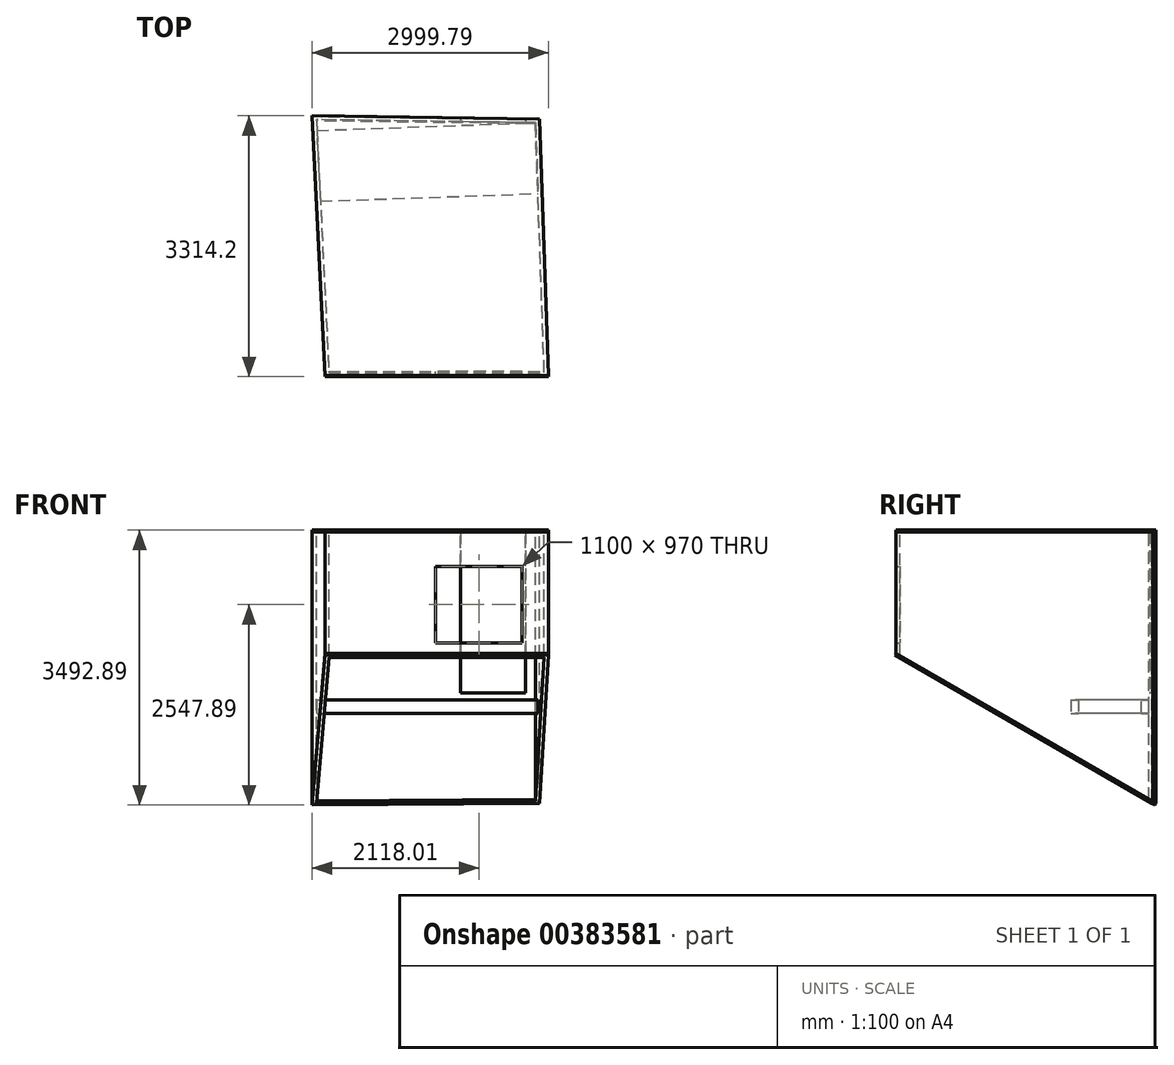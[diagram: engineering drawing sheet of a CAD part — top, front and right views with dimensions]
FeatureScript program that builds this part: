
annotation { "Feature Type Name" : "Feature", "Feature Type Description" : "" }
export const myFeature = defineFeature(function(context is Context, id is Id, definition is map)
    precondition{}
    {
        {
            var Q0;
            Q0=qCreatedBy(makeId("Top.planeOp"),FACE);
            var sketch = newSketch(context, id + "F0", { "sketchPlane" : qUnion([Q0])});
            skLineSegment(sketch, "E0", {"start": v(0, 0) * mm, "end": v(2735, 0) * mm});
            skLineSegment(sketch, "E1", {"start": v(2735, 0) * mm, "end": v(2624.33, 3163.06) * mm});
            skLineSegment(sketch, "E2", {"start": v(2624.33, 3163.06) * mm, "end": v(-160.4, 3200.98) * mm});
            skLineSegment(sketch, "E3", {"start": v(-160.4, 3200.98) * mm, "end": v(0, 0) * mm});
            skLineSegment(sketch, "E4", {"start": v(2624.33, 3163.06) * mm, "end": v(0, 0) * mm, "construction": true});
            skLineSegment(sketch, "E5.0", {"start": v(-47.56, -50) * mm, "end": v(2786.78, -50) * mm});
            skLineSegment(sketch, "E5.1", {"start": v(-213.01, 3251.7) * mm, "end": v(-47.56, -50) * mm});
            skLineSegment(sketch, "E5.2", {"start": v(2672.64, 3212.41) * mm, "end": v(-213.01, 3251.7) * mm});
            skLineSegment(sketch, "E5.3", {"start": v(2786.78, -50) * mm, "end": v(2672.64, 3212.41) * mm});
            skSolve(sketch);
        }
        {
            var Q0;
            Q0=makeQuery(id+"F0.imprint","IMPRINT",FACE,{"disambiguationData":[TD([[makeQuery(id+"F0.imprint","IMPRINT",EDGE,{"derivedFrom":sQuery(id+"F0.wireOp",EDGE,"E0")}),-1.0]])]});
            extrude(context, id + "F1", {"entities" : qUnion([Q0]), "oppositeDirection" : true, "depth" : 4110 * mm});
        }
        {
            var Q0;
            Q0=makeQuery(id+"F1.opExtrude","SWEPT_FACE",FACE,{"disambiguationData":[OSD([sQuery(id+"F0.wireOp",EDGE,"E5.0")])]});
            var sketch = newSketch(context, id + "F2", { "sketchPlane" : qUnion([Q0])});
            skLineSegment(sketch, "E6", {"start": v(-47.56, -1540) * mm, "end": v(2786.78, -1540) * mm});
            skSolve(sketch);
        }
        {
            var Q0;
            Q0=sQuery(id+"F2.wireOp",EDGE,"E6");
            cPlane(context, id + "F3", {"entities" : qUnion([Q0]), "cplaneType" : CPlaneType.LINE_ANGLE, "offset" : 25 * mm, "angle" : 30 * degree, "oppositeDirection" : true, "width" : 150 * mm, "height" : 150 * mm});
        }
        {
            var Q0;
            Q0=qCreatedBy(id+"F3.planeOp",FACE);
            var sketch = newSketch(context, id + "F4", { "sketchPlane" : qUnion([Q0])});
            skLineSegment(sketch, "E7.0", {"start": v(47.56, -1358.68) * mm, "end": v(-2786.78, -1358.68) * mm});
            skLineSegment(sketch, "E8.bottom", {"start": v(-2786.78, -1358.68) * mm, "end": v(1857.9, -1358.68) * mm});
            skLineSegment(sketch, "E8.top", {"start": v(-2786.78, -4651.7) * mm, "end": v(1857.9, -4651.7) * mm});
            skLineSegment(sketch, "E8.left", {"start": v(-2786.78, -1358.68) * mm, "end": v(-2786.78, -4651.7) * mm});
            skLineSegment(sketch, "E8.right", {"start": v(1857.9, -1358.68) * mm, "end": v(1857.9, -4651.7) * mm});
            skSolve(sketch);
        }
        {
            var Q0;
            Q0=makeQuery(id+"F4.imprint","IMPRINT",FACE,{"disambiguationData":[TD([[makeQuery(id+"F4.imprint","IMPRINT",EDGE,{"derivedFrom":sQuery(id+"F4.wireOp",EDGE,"E8.top")}),1.0]])]});
            extrude(context, id + "F5", {"entities" : qUnion([Q0]), "operationType" : NewBodyOperationType.REMOVE, "endBound" : BoundingType.THROUGH_ALL, "depth" : 25 * mm});
        }
        {
            var Q0;
            Q0=makeQuery(id+"F0.imprint","IMPRINT",FACE,{"disambiguationData":[TD([[makeQuery(id+"F0.imprint","IMPRINT",EDGE,{"derivedFrom":sQuery(id+"F0.wireOp",EDGE,"E0")}),1.0]])]});
            var Q1;
            Q1=makeQuery(id+"F0.imprint","IMPRINT",FACE,{"disambiguationData":[TD([[makeQuery(id+"F0.imprint","IMPRINT",EDGE,{"derivedFrom":sQuery(id+"F0.wireOp",EDGE,"E0")}),-1.0]])]});
            extrude(context, id + "F6", {"entities" : qUnion([Q0, Q1]), "depth" : 25 * mm});
        }
        {
            var Q0;
            Q0=makeQuery(id+"F5.boolean.opBoolean","COPY",FACE,{"derivedFrom":makeQuery(id+"F5.opExtrude","SWEPT_FACE",FACE,{"disambiguationData":[OSD([sQuery(id+"F4.wireOp",EDGE,"E8.bottom")])]})});
            var sketch = newSketch(context, id + "F7", { "sketchPlane" : qUnion([Q0])});
            skLineSegment(sketch, "E9", {"start": v(2672.64, -4493.8) * mm, "end": v(-213.01, -4539.18) * mm});
            skLineSegment(sketch, "E10", {"start": v(-213.01, -4539.18) * mm, "end": v(-47.56, -726.7) * mm});
            skLineSegment(sketch, "E11", {"start": v(-47.56, -726.7) * mm, "end": v(2786.78, -726.7) * mm});
            skLineSegment(sketch, "E12", {"start": v(2786.78, -726.7) * mm, "end": v(2672.64, -4493.8) * mm});
            skLineSegment(sketch, "E13.0", {"start": v(2624.33, -4436.83) * mm, "end": v(2735, -784.43) * mm});
            skLineSegment(sketch, "E14.0", {"start": v(-160.4, -4480.61) * mm, "end": v(2624.33, -4436.83) * mm});
            skLineSegment(sketch, "E15.0", {"start": v(0, -784.43) * mm, "end": v(-160.4, -4480.61) * mm});
            skLineSegment(sketch, "E16.0", {"start": v(2735, -784.43) * mm, "end": v(0, -784.43) * mm});
            skSolve(sketch);
        }
        {
            var Q0;
            Q0=makeQuery(id+"F7.imprint","IMPRINT",FACE,{"disambiguationData":[TD([[makeQuery(id+"F7.imprint","IMPRINT",EDGE,{"derivedFrom":sQuery(id+"F7.wireOp",EDGE,"E13.0")}),1.0]])]});
            var Q1;
            Q1=makeQuery(id+"F7.imprint","IMPRINT",FACE,{"disambiguationData":[TD([[makeQuery(id+"F7.imprint","IMPRINT",EDGE,{"derivedFrom":sQuery(id+"F7.wireOp",EDGE,"E9")}),1.0]])]});
            extrude(context, id + "F8", {"entities" : qUnion([Q0, Q1]), "depth" : 25 * mm});
        }
        {
            var Q0;
            Q0=makeQuery(id+"F1.opExtrude","SWEPT_FACE",FACE,{"disambiguationData":[OSD([sQuery(id+"F0.wireOp",EDGE,"E2")])]});
            var sketch = newSketch(context, id + "F9", { "sketchPlane" : qUnion([Q0])});
            skLineSegment(sketch, "E17.bottom", {"start": v(2456.02, 0) * mm, "end": v(1626.02, 0) * mm});
            skLineSegment(sketch, "E17.top", {"start": v(2456.02, -2040) * mm, "end": v(1626.02, -2040) * mm});
            skLineSegment(sketch, "E17.left", {"start": v(2456.02, 0) * mm, "end": v(2456.02, -2040) * mm});
            skLineSegment(sketch, "E17.right", {"start": v(1626.02, 0) * mm, "end": v(1626.02, -2040) * mm});
            skSolve(sketch);
        }
        {
            var Q0;
            Q0=makeQuery(id+"F9.imprint","IMPRINT",FACE,{"disambiguationData":[TD([[makeQuery(id+"F9.imprint","IMPRINT",EDGE,{"derivedFrom":sQuery(id+"F9.wireOp",EDGE,"E17.bottom")}),1.0]])]});
            extrude(context, id + "F10", {"entities" : qUnion([Q0]), "operationType" : NewBodyOperationType.REMOVE, "endBound" : BoundingType.THROUGH_ALL, "oppositeDirection" : true, "depth" : 25 * mm});
        }
        {
            var Q0;
            Q0=makeQuery(id+"F9.imprint","IMPRINT",FACE,{"disambiguationData":[TD([[makeQuery(id+"F9.imprint","IMPRINT",EDGE,{"derivedFrom":sQuery(id+"F9.wireOp",EDGE,"E17.bottom")}),1.0]])]});
            var Q1;
            {var subQ0=sQuery(id+"F0.wireOp",EDGE,"E5.2");Q1=makeQuery(id+"F6.boolean.opBoolean","MERGE",FACE,{"derivedFrom":[makeQuery(id+"F1.opExtrude","SWEPT_FACE",FACE,{"disambiguationData":[OSD([subQ0])]}),makeQuery(id+"F6.opExtrude","SWEPT_FACE",FACE,{"disambiguationData":[OSD([subQ0])]})]});}
            extrude(context, id + "F11", {"entities" : qUnion([Q0]), "endBound" : BoundingType.UP_TO_SURFACE, "oppositeDirection" : true, "endBoundEntityFace" : qUnion([Q1]), "depth" : 25 * mm});
        }
        {
            var Q0;
            Q0=makeQuery(id+"F1.opExtrude","SWEPT_FACE",FACE,{"disambiguationData":[OSD([sQuery(id+"F0.wireOp",EDGE,"E1")])]});
            var sketch = newSketch(context, id + "F12", { "sketchPlane" : qUnion([Q0])});
            skLineSegment(sketch, "E18.bottom", {"start": v(-3069.37, -2130) * mm, "end": v(-2169.37, -2130) * mm});
            skLineSegment(sketch, "E18.top", {"start": v(-3069.37, -2300) * mm, "end": v(-2169.37, -2300) * mm});
            skLineSegment(sketch, "E18.left", {"start": v(-3069.37, -2130) * mm, "end": v(-3069.37, -2300) * mm});
            skLineSegment(sketch, "E18.right", {"start": v(-2169.37, -2130) * mm, "end": v(-2169.37, -2300) * mm});
            skSolve(sketch);
        }
        {
            var Q0;
            Q0=makeQuery(id+"F12.imprint","IMPRINT",FACE,{"disambiguationData":[TD([[makeQuery(id+"F12.imprint","IMPRINT",EDGE,{"derivedFrom":sQuery(id+"F12.wireOp",EDGE,"E18.bottom")}),-1.0]])]});
            var Q1;
            Q1=makeQuery(id+"F1.opExtrude","SWEPT_FACE",FACE,{"disambiguationData":[OSD([sQuery(id+"F0.wireOp",EDGE,"E3")])]});
            extrude(context, id + "F13", {"entities" : qUnion([Q0]), "endBound" : BoundingType.UP_TO_SURFACE, "endBoundEntityFace" : qUnion([Q1]), "depth" : 25 * mm});
        }
        {
            var Q0;
            Q0=makeQuery(id+"F1.opExtrude","SWEPT_FACE",FACE,{"disambiguationData":[OSD([sQuery(id+"F0.wireOp",EDGE,"E0")])]});
            var sketch = newSketch(context, id + "F14", { "sketchPlane" : qUnion([Q0])});
            skLineSegment(sketch, "E19.bottom", {"start": v(-2455, -435) * mm, "end": v(-1355, -435) * mm});
            skLineSegment(sketch, "E19.top", {"start": v(-2455, -1405) * mm, "end": v(-1355, -1405) * mm});
            skLineSegment(sketch, "E19.left", {"start": v(-2455, -435) * mm, "end": v(-2455, -1405) * mm});
            skLineSegment(sketch, "E19.right", {"start": v(-1355, -435) * mm, "end": v(-1355, -1405) * mm});
            skSolve(sketch);
        }
        {
            var Q0;
            Q0 = qSketchRegion(id + "F14", true);
            extrude(context, id + "F15", {"entities" : qUnion([Q0]), "operationType" : NewBodyOperationType.REMOVE, "endBound" : BoundingType.THROUGH_ALL, "oppositeDirection" : true, "depth" : 590 * mm});
        }
    });
